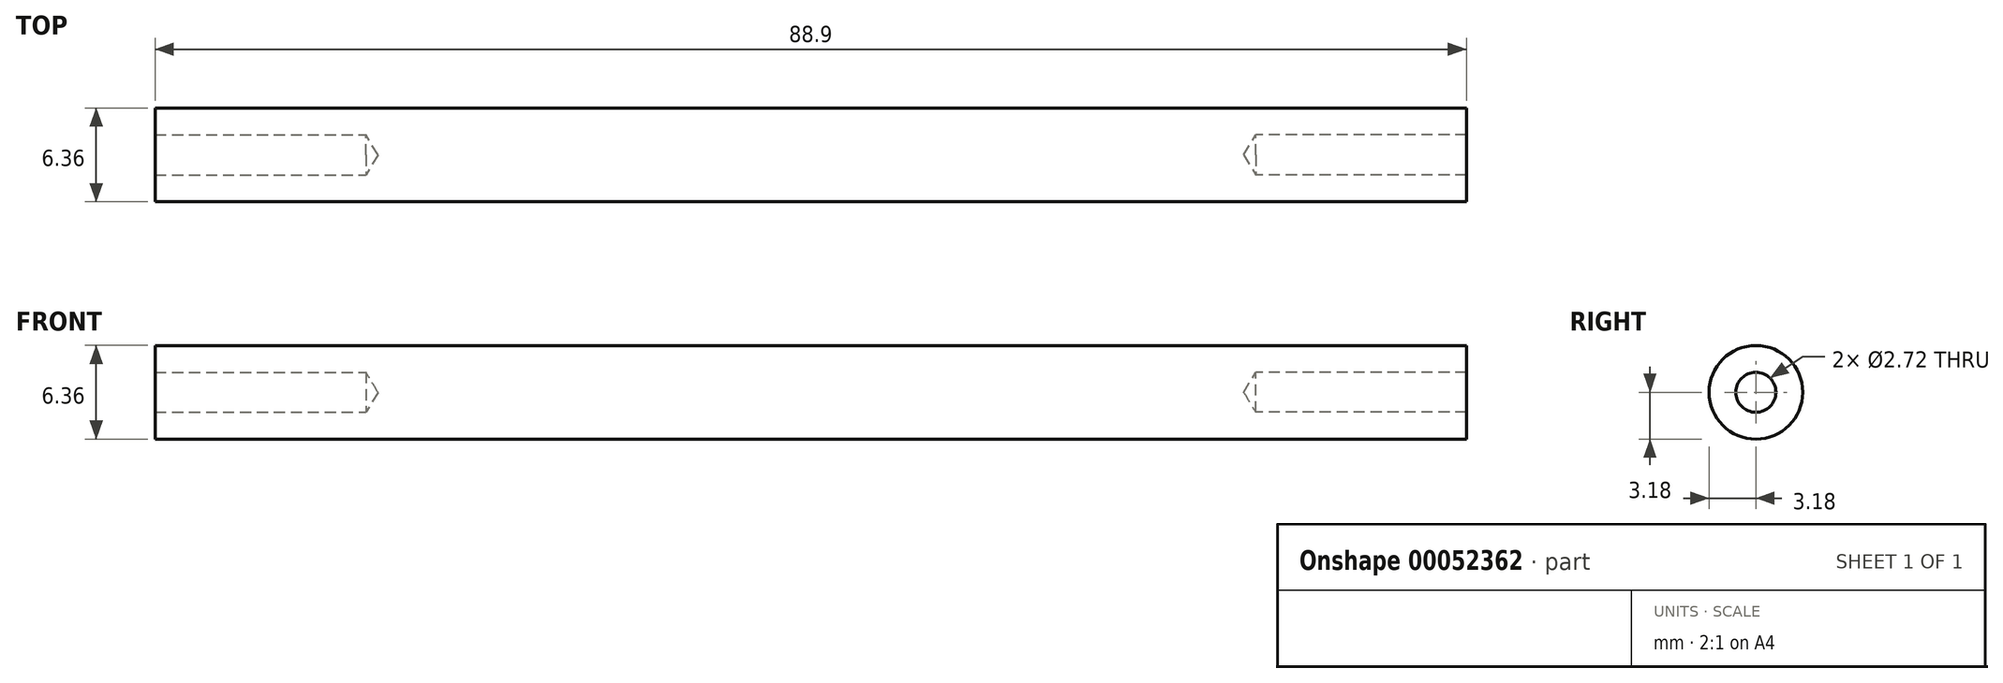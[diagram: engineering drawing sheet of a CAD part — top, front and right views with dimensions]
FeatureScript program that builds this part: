
annotation { "Feature Type Name" : "Feature", "Feature Type Description" : "" }
export const myFeature = defineFeature(function(context is Context, id is Id, definition is map)
    precondition{}
    {
        {
            var Q0;
            Q0=qCreatedBy(makeId("Right.planeOp"),FACE);
            var sketch = newSketch(context, id + "F0", { "sketchPlane" : qUnion([Q0])});
            skCircle(sketch, "E0", {"center": v(0, 0) * mm, "radius": 3.18 * mm});
            skSolve(sketch);
        }
        {
            var Q0;
            Q0 = qSketchRegion(id + "F0", true);
            extrude(context, id + "F1", {"entities" : qUnion([Q0]), "depth" : 88.9 * mm, "symmetric" : true});
        }
        {
            var Q0;
            Q0=makeQuery(id+"F1.opExtrude","CAP_FACE",FACE,{"disambiguationData":[OSD([sQuery(id+"F0.wireOp",EDGE,"E0")])],"isStart":false});
            var sketch = newSketch(context, id + "F2", { "sketchPlane" : qUnion([Q0])});
            skPoint(sketch, "E1", {"position": v(0, 0) * mm});
            skSolve(sketch);
        }
        {
            var Q0;
            Q0=makeQuery(id+"F1.opExtrude","CAP_FACE",FACE,{"disambiguationData":[OSD([sQuery(id+"F0.wireOp",EDGE,"E0")])],"isStart":true});
            var sketch = newSketch(context, id + "F3", { "sketchPlane" : qUnion([Q0])});
            skPoint(sketch, "E2", {"position": v(0, 0) * mm});
            skSolve(sketch);
        }
        {
            var Q0;
            Q0=sQuery(id+"F3.wireOp",VERTEX,"E2");
            var Q1;
            Q1=sQuery(id+"F2.wireOp",VERTEX,"E1");
            var Q2;
            Q2=makeQuery(id+"F1.opExtrude","SWEPT_BODY",BODY,{"disambiguationData":[OSD([sQuery(id+"F0.wireOp",EDGE,"E0")])]});
            hole(context, id + "F4", {"style" : HoleStyle.SIMPLE, "holeDiameter" : 2.72 * mm, "endStyle" : HoleEndStyle.BLIND, "holeDepth" : 14.29 * mm, "locations" : qUnion([Q0, Q1]), "scope" : qUnion([Q2])});
        }
    });
